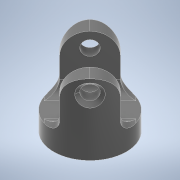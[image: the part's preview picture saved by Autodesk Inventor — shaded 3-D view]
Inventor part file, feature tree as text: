
AUTODESK INVENTOR PART (.ipt)
format: ipt  version: 2022 (Build 260153000, 153)  size: 203,776 bytes
history: native  units: in
note: dims shown in document units (in); Inventor stores cm internally (conversion verified against a paired STEP export)
features: sketch x3, extrude x2, fillet x2, hole x1, chamfer x1, pattern_circular x1
ambient origin geometry x8: Origin, YZ Plane, XZ Plane, XY Plane, X Axis, Y Axis, Z Axis, Center Point
bodies: Solid1 (feature_tree)
feature tree (10):
  extrude  "Extrusion1"  Depth=0.1969in TaperAngle=0.0deg
  extrude  "Extrusion2"  Depth=0.0787in
  fillet  "Fillet1"  [1 undecoded]
  hole  "Hole1"  [1 undecoded]
  chamfer  "Chamfer1"  Distance=0.5709in
  pattern_circular  "Circular Pattern2"  [2 undecoded]
  fillet  "Fillet5"  Radius=0.2335in
  sketch  "Sketch1"  dims[d0=0.7874in d1=0.1969in d2=0.0in]
  sketch  "Sketch2"  dims[d3=45.0deg d4=0.0787in d5=45.0deg]
  sketch  "Sketch4"  dims[d6=0.0787in d7=45.0deg d8=0.5709in d9=0.0in d11=0.1575in d12=0.2362in d13=0.1575in d14=0.0787in d15=90.0deg d16=0.1181in d17=0.0in d18=0.1575in d19=0.2335in d20=0.0394in d21=0.0787in d22=45.0deg d26=0.1181in d30=0.7874in d31=360.0deg d33=0.2335in d10=0.0787in d34=0.0in d35=0.0in d36=0.0in]
note: 4 required parameter values undecoded (feature->parameter linkage not recoverable at this tier; creation-order binding heuristic only, values carry confidence <= 0.55)
